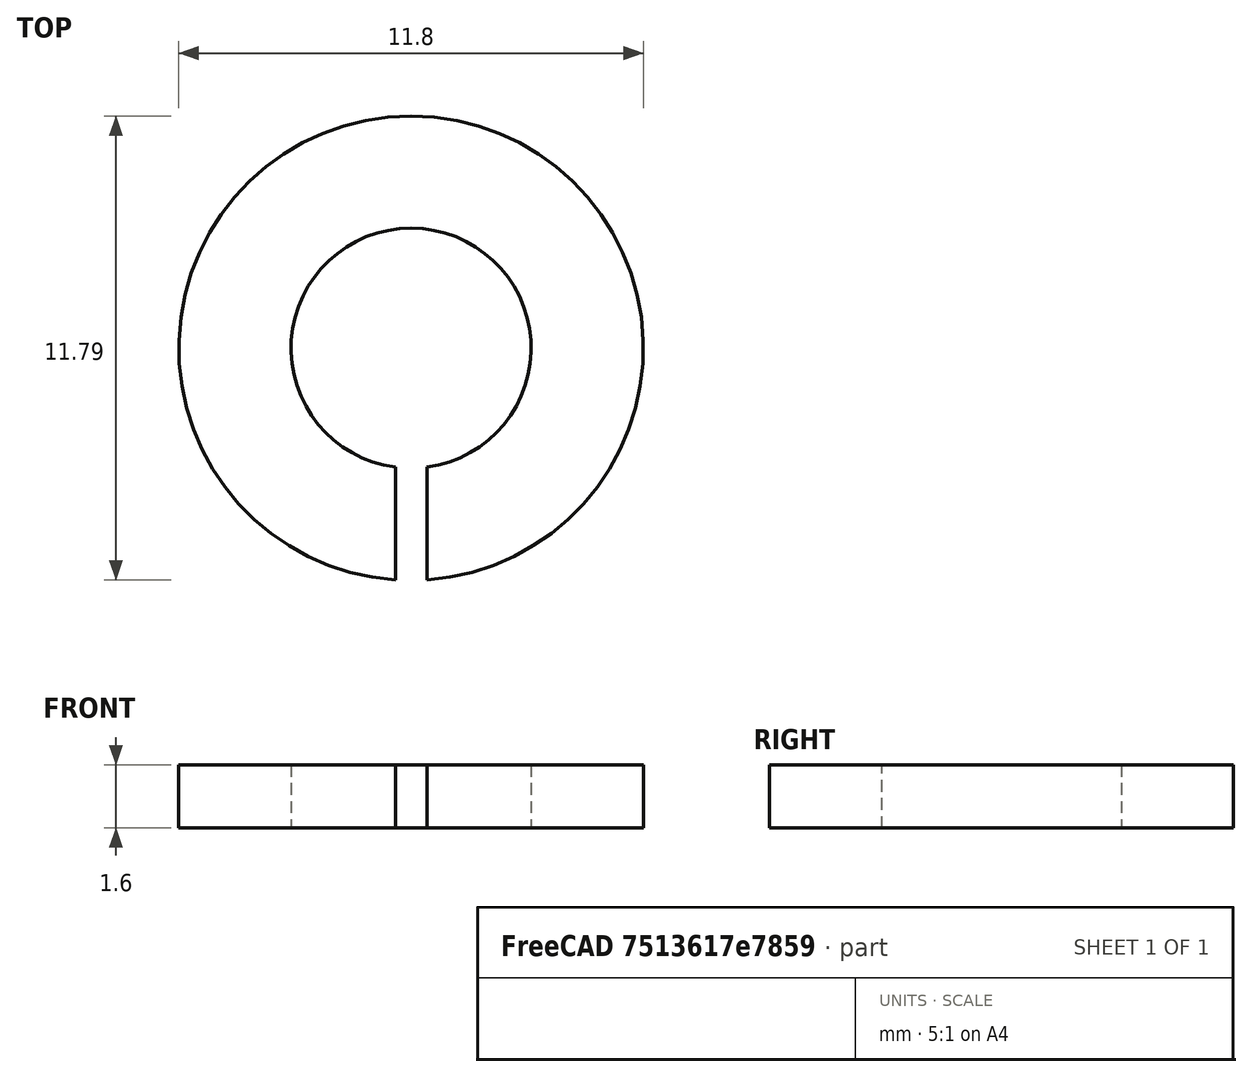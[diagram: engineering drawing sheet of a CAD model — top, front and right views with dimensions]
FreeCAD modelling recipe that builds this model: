
FCSTD DOCUMENT  (FreeCAD 0.15R4651 (Git))
Label: Federring_DIN127-B6
License: All rights reserved
LicenseURL: http://de.wikipedia.org/wiki/Alle_Rechte_vorbehalten
objects: Sketcher::SketchObject×1, PartDesign::Pad×1
note: 3 computed .brp shape members not serialized (recipe doc carries the construction recipe); baked Part::Feature solids carry a one-line shape summary decoded from their .brp

FEATURE [Sketcher::SketchObject] Sketch
  sketch-geometry (4):
    g0: ArcOfCircle CenterX=0 CenterY=0 CenterZ=0 NormalX=0 NormalY=0 NormalZ=1 Radius=3.05 StartAngle=4.84392 EndAngle=10.864
    g1: ArcOfCircle CenterX=0 CenterY=0 CenterZ=0 NormalX=0 NormalY=0 NormalZ=1 Radius=5.9 StartAngle=4.78024 EndAngle=10.9277
    g2: LineSegment StartX=0.4 StartY=-3.02366 StartZ=0 EndX=0.4 EndY=-5.88643 EndZ=0
    g3: LineSegment StartX=-0.4 StartY=-5.88643 StartZ=0 EndX=-0.4 EndY=-3.02366 EndZ=0
  constraints (12):
    c: Coincident(g0,g-1)
    c: Coincident(g1,g-1)
    c: Vertical(g2)
    c: Vertical(g3)
    c: Coincident(g0,g2)
    c: Coincident(g0,g3)
    c: Coincident(g1,g2)
    c: Coincident(g1,g3)
    c: Symmetric(g1,g1,g-2)
    c: Radius(g0) = 3.05
    c: Radius(g1) = 5.9
    c: DistanceX(g1,g1) = -0.8
FEATURE [PartDesign::Pad] Pad  label="Federring DIN 127-B 6 #"
  Length = 1.6
  Length2 = 100
  Midplane = true
  Sketch = -> Sketch
  Type = 0
